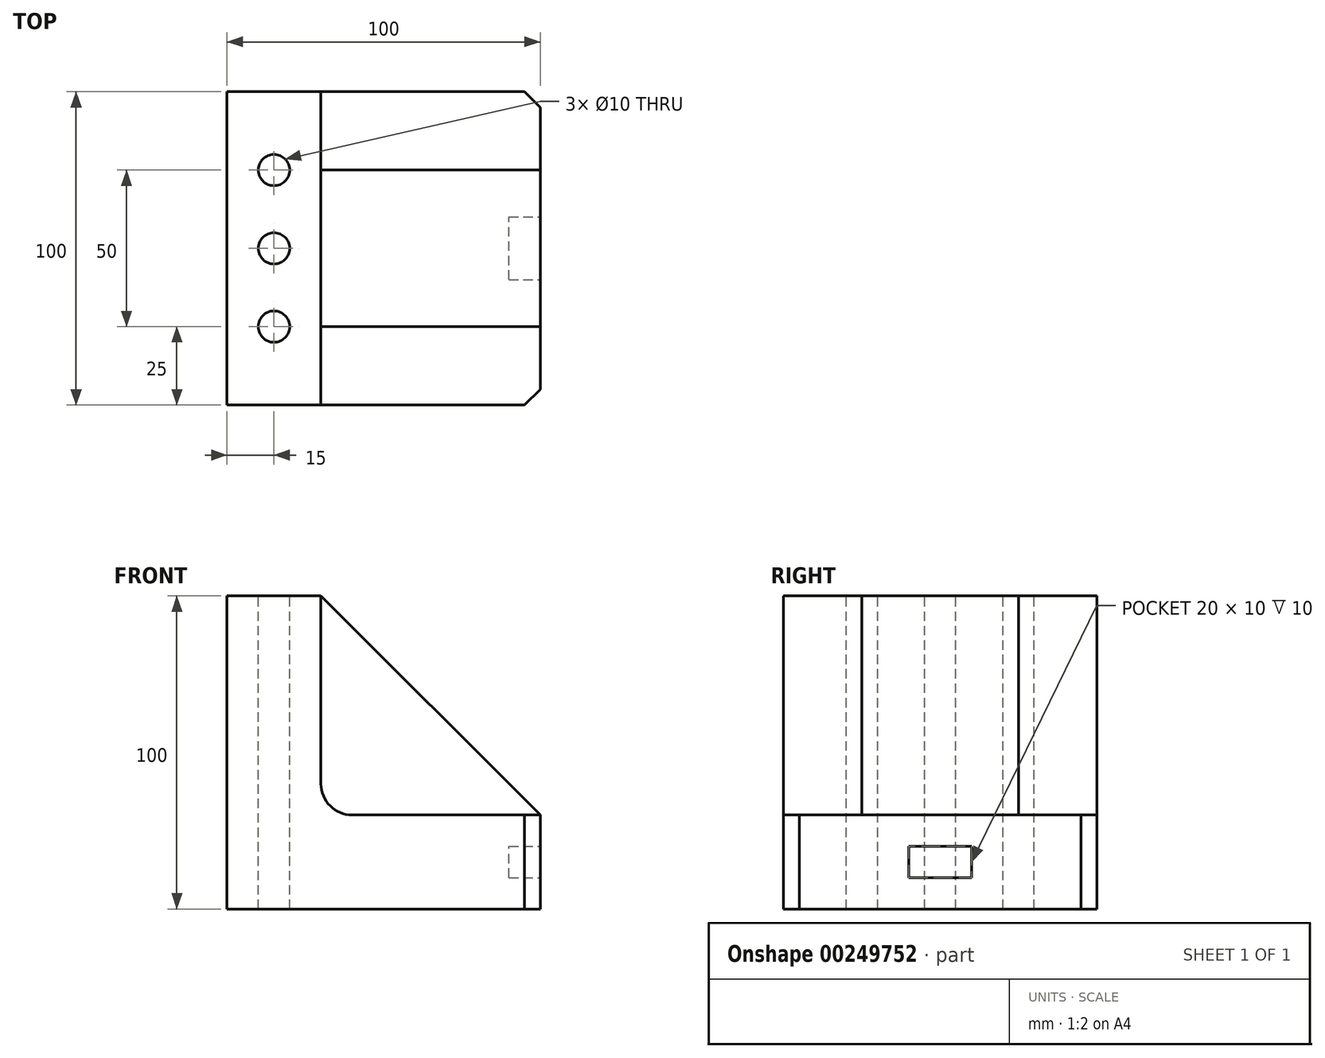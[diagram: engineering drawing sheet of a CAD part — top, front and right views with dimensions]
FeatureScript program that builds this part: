
annotation { "Feature Type Name" : "Feature", "Feature Type Description" : "" }
export const myFeature = defineFeature(function(context is Context, id is Id, definition is map)
    precondition{}
    {
        {
            var Q0;
            Q0=qCreatedBy(makeId("Top.planeOp"),FACE);
            var sketch = newSketch(context, id + "F0", { "sketchPlane" : qUnion([Q0])});
            skLineSegment(sketch, "E0.bottom", {"start": v(0, 0) * mm, "end": v(100, 0) * mm});
            skLineSegment(sketch, "E0.top", {"start": v(0, 100) * mm, "end": v(100, 100) * mm});
            skLineSegment(sketch, "E0.left", {"start": v(0, 0) * mm, "end": v(0, 100) * mm});
            skLineSegment(sketch, "E0.right", {"start": v(100, 0) * mm, "end": v(100, 100) * mm});
            skSolve(sketch);
        }
        {
            var Q0;
            Q0 = qSketchRegion(id + "F0", true);
            extrude(context, id + "F1", {"entities" : qUnion([Q0]), "depth" : 100 * mm});
        }
        {
            var Q0;
            Q0=makeQuery(id+"F1.opExtrude","SWEPT_FACE",FACE,{"disambiguationData":[OSD([sQuery(id+"F0.wireOp",EDGE,"E0.right")])]});
            var sketch = newSketch(context, id + "F2", { "sketchPlane" : qUnion([Q0])});
            skLineSegment(sketch, "E1.bottom", {"start": v(40, 10) * mm, "end": v(60, 10) * mm});
            skLineSegment(sketch, "E1.top", {"start": v(40, 20) * mm, "end": v(60, 20) * mm});
            skLineSegment(sketch, "E1.left", {"start": v(40, 10) * mm, "end": v(40, 20) * mm});
            skLineSegment(sketch, "E1.right", {"start": v(60, 10) * mm, "end": v(60, 20) * mm});
            skSolve(sketch);
        }
        {
            var Q0;
            Q0 = qSketchRegion(id + "F2", true);
            extrude(context, id + "F3", {"entities" : qUnion([Q0]), "operationType" : NewBodyOperationType.REMOVE, "oppositeDirection" : true, "depth" : 10 * mm});
        }
        {
            var Q0;
            Q0=makeQuery(id+"F1.opExtrude","CAP_FACE",FACE,{"disambiguationData":[OSD([sQuery(id+"F0.wireOp",EDGE,"E0.bottom"),sQuery(id+"F0.wireOp",EDGE,"E0.top"),sQuery(id+"F0.wireOp",EDGE,"E0.left"),sQuery(id+"F0.wireOp",EDGE,"E0.right")])],"isStart":false});
            var sketch = newSketch(context, id + "F4", { "sketchPlane" : qUnion([Q0])});
            skCircle(sketch, "E2", {"center": v(15, 75) * mm, "radius": 5 * mm});
            skCircle(sketch, "E3.0.1.0", {"center": v(15, 50) * mm, "radius": 5 * mm});
            skCircle(sketch, "E3.0.2.0", {"center": v(15, 25) * mm, "radius": 5 * mm});
            skLineSegment(sketch, "E3.direction1", {"start": v(15, 75) * mm, "end": v(34, 75) * mm, "construction": true});
            skLineSegment(sketch, "E3.direction2", {"start": v(15, 75) * mm, "end": v(15, 50) * mm, "construction": true});
            skSolve(sketch);
        }
        {
            var Q0;
            Q0 = qSketchRegion(id + "F4", true);
            extrude(context, id + "F5", {"entities" : qUnion([Q0]), "operationType" : NewBodyOperationType.REMOVE, "endBound" : BoundingType.THROUGH_ALL, "oppositeDirection" : true, "depth" : 25 * mm});
        }
        {
            var Q0;
            Q0=makeQuery(id+"F1.opExtrude","SWEPT_FACE",FACE,{"disambiguationData":[OSD([sQuery(id+"F0.wireOp",EDGE,"E0.bottom")])]});
            var sketch = newSketch(context, id + "F6", { "sketchPlane" : qUnion([Q0])});
            skLineSegment(sketch, "E4", {"start": v(100, 100) * mm, "end": v(30, 100) * mm});
            skLineSegment(sketch, "E5", {"start": v(30, 100) * mm, "end": v(100, 30) * mm});
            skLineSegment(sketch, "E6", {"start": v(100, 30) * mm, "end": v(100, 100) * mm});
            skSolve(sketch);
        }
        {
            var Q0;
            Q0 = qSketchRegion(id + "F6", true);
            extrude(context, id + "F7", {"entities" : qUnion([Q0]), "operationType" : NewBodyOperationType.REMOVE, "endBound" : BoundingType.THROUGH_ALL, "oppositeDirection" : true, "depth" : 25 * mm});
        }
        {
            var Q0;
            Q0=makeQuery(id+"F1.opExtrude","SWEPT_FACE",FACE,{"disambiguationData":[OSD([sQuery(id+"F0.wireOp",EDGE,"E0.bottom")])]});
            var sketch = newSketch(context, id + "F8", { "sketchPlane" : qUnion([Q0])});
            skLineSegment(sketch, "E7", {"start": v(30, 100) * mm, "end": v(30, 30) * mm});
            skLineSegment(sketch, "E8", {"start": v(30, 30) * mm, "end": v(100, 30) * mm});
            skLineSegment(sketch, "E9", {"start": v(100, 30) * mm, "end": v(30, 100) * mm});
            skSolve(sketch);
        }
        {
            var Q0;
            Q0 = qSketchRegion(id + "F8", true);
            extrude(context, id + "F9", {"entities" : qUnion([Q0]), "operationType" : NewBodyOperationType.REMOVE, "oppositeDirection" : true, "depth" : 25 * mm});
        }
        {
            var Q0;
            Q0=makeQuery(id+"F1.opExtrude","SWEPT_FACE",FACE,{"disambiguationData":[OSD([sQuery(id+"F0.wireOp",EDGE,"E0.top")])]});
            var sketch = newSketch(context, id + "F10", { "sketchPlane" : qUnion([Q0])});
            skLineSegment(sketch, "E10", {"start": v(-100, 30) * mm, "end": v(-30, 30) * mm});
            skLineSegment(sketch, "E11", {"start": v(-30, 30) * mm, "end": v(-30, 100) * mm});
            skLineSegment(sketch, "E12", {"start": v(-30, 100) * mm, "end": v(-100, 30) * mm});
            skSolve(sketch);
        }
        {
            var Q0;
            Q0 = qSketchRegion(id + "F10", true);
            extrude(context, id + "F11", {"entities" : qUnion([Q0]), "operationType" : NewBodyOperationType.REMOVE, "oppositeDirection" : true, "depth" : 25 * mm});
        }
        {
            var Q0;
            Q0=makeQuery(id+"F9.boolean.opBoolean","COPY",EDGE,{"derivedFrom":makeQuery(id+"F9.opExtrude","SWEPT_EDGE",EDGE,{"disambiguationData":[OSD([sQuery(id+"F8.wireOp",EDGE,"E7"),sQuery(id+"F8.wireOp",EDGE,"E8")])]})});
            var Q1;
            Q1=makeQuery(id+"F11.boolean.opBoolean","COPY",EDGE,{"derivedFrom":makeQuery(id+"F11.opExtrude","SWEPT_EDGE",EDGE,{"disambiguationData":[OSD([sQuery(id+"F10.wireOp",EDGE,"E10"),sQuery(id+"F10.wireOp",EDGE,"E11")])]})});
            fillet(context, id + "F12", {"entities" : qUnion([Q0, Q1]), "radius" : 10 * mm, "tangentPropagation" : true, "allowEdgeOverflow" : false});
        }
        {
            var Q0;
            Q0=makeQuery(id+"F1.opExtrude","SWEPT_EDGE",EDGE,{"disambiguationData":[OSD([sQuery(id+"F0.wireOp",EDGE,"E0.bottom"),sQuery(id+"F0.wireOp",EDGE,"E0.right")])]});
            var Q1;
            Q1=makeQuery(id+"F1.opExtrude","SWEPT_EDGE",EDGE,{"disambiguationData":[OSD([sQuery(id+"F0.wireOp",EDGE,"E0.top"),sQuery(id+"F0.wireOp",EDGE,"E0.right")])]});
            chamfer(context, id + "F13", {"entities" : qUnion([Q0, Q1]), "width" : 5 * mm, "tangentPropagation" : true});
        }
    });
